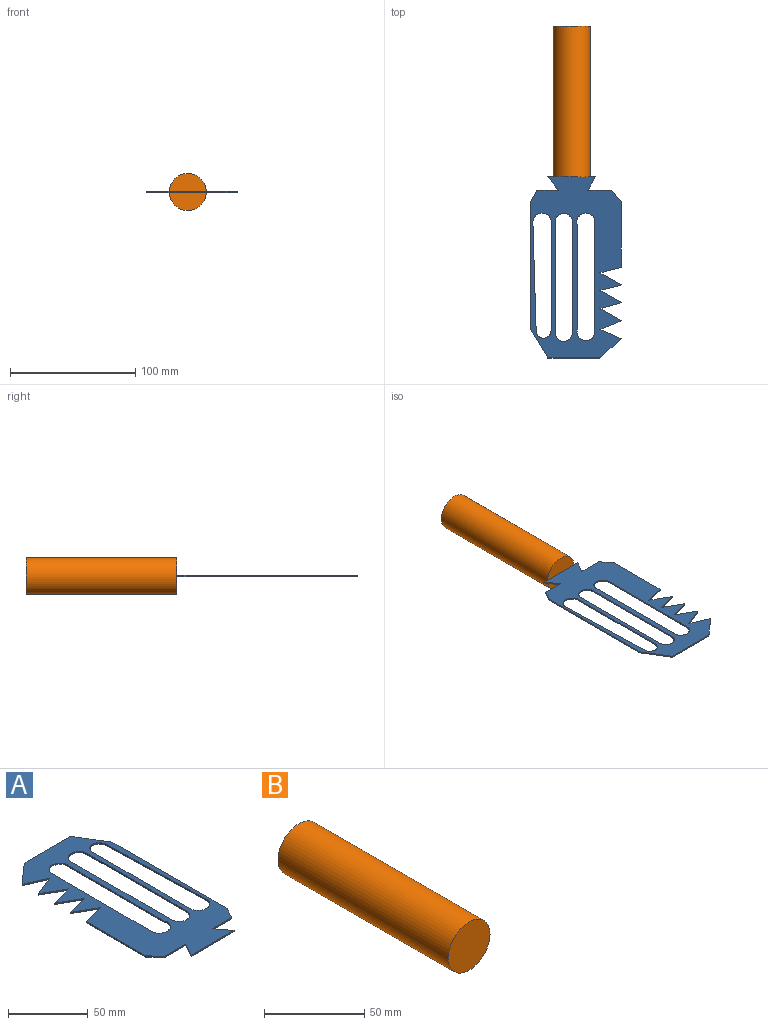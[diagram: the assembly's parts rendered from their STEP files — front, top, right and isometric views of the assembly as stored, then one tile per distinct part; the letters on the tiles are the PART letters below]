
ASSEMBLY  parts=2 mates=1
PART A: 34 faces, bbox 72.3x144.6x1 mm
  f0: plane 144.64x72.27mm, normal (0,0,1), area 5191.7mm2, adj f2,f3,f4,f5,f6,f7,f8,f9
  f1: plane 144.64x72.27mm, normal (0,0,-1), area 5191.7mm2, adj f2,f3,f4,f5,f6,f7,f8,f9
  f2: plane 8.78x4.98mm, normal (0.87,-0.49,0), area 10.1mm2, adj f0,f1,f3,f21
  f3: plane 102.2x1mm, normal (1,0,0), area 102.2mm2, adj f0,f1,f2,f4
  f4: plane 22.72x13.76mm, normal (0.86,0.52,0), area 26.6mm2, adj f0,f1,f3,f5
  f5: plane 41.27x1mm, normal (0,1,0), area 41.3mm2, adj f0,f1,f4,f6
  f6: plane 17.25x15.22mm, normal (-0.66,0.75,0), area 23mm2, adj f0,f1,f5,f7
  f7: plane 17.02x7.5mm, normal (-0.4,-0.91,0), area 18.6mm2, adj f0,f1,f6,f8
  f8: plane 17.02x6.98mm, normal (-0.38,0.93,0), area 18.4mm2, adj f0,f1,f7,f9
  f9: plane 17.02x9.65mm, normal (-0.49,-0.87,0), area 19.6mm2, adj f0,f1,f8,f10
  f10: plane 17.02x4.83mm, normal (-0.27,0.96,0), area 17.7mm2, adj f0,f1,f9,f11
  f11: plane 17.02x9.65mm, normal (-0.49,-0.87,0), area 19.6mm2, adj f0,f1,f10,f12
  f12: plane 17.02x4.39mm, normal (-0.25,0.97,0), area 17.6mm2, adj f0,f1,f11,f13
  f13: plane 17.02x9.65mm, normal (-0.49,-0.87,0), area 19.6mm2, adj f0,f1,f12,f14
  f14: plane 17.02x4.44mm, normal (-0.25,0.97,0), area 17.6mm2, adj f0,f1,f13,f15
  f15: plane 52.6x1mm, normal (-1,0,0), area 52.6mm2, adj f0,f1,f14,f16
  f16: plane 8.78x7.8mm, normal (-0.75,-0.66,0), area 11.7mm2, adj f0,f1,f15,f17
  f17: plane 18.92x1mm, normal (0,-1,0), area 18.9mm2, adj f0,f1,f16,f18
  f18: plane 10.94x6.21mm, normal (-0.87,0.49,0), area 12.6mm2, adj f0,f1,f17,f19
  f19: plane 38x1mm, normal (0,-1,0), area 38mm2, adj f0,f1,f18,f20
  f20: plane 10.94x8.15mm, normal (0.8,0.6,0), area 13.6mm2, adj f0,f1,f19,f21
  f21: plane 16.93x1mm, normal (0,-1,0), area 16.9mm2, adj f0,f1,f2,f20
  f22: plane 89.33x1mm, normal (-1,0,0), area 89.3mm2, adj f0,f1,f23,f25
  f23: cylinder r=6.78mm len=13.55mm, axis (0,0,1), area 21.3mm2, adj f0,f1,f22,f24
  f24: plane 89.33x1mm, normal (1,0,0), area 89.3mm2, adj f0,f1,f23,f25
  f25: cylinder r=6.86mm len=13.55mm, axis (0,0,1), area 19.4mm2, adj f0,f1,f22,f24
  f26: plane 85.09x2.57mm, normal (-1,-0.03,0), area 85.1mm2, adj f0,f1,f27,f29
  f27: cylinder r=5.97mm len=11.95mm, axis (0,0,1), area 19.7mm2, adj f0,f1,f26,f28
  f28: plane 86.18x1mm, normal (1,0,0), area 86.2mm2, adj f0,f1,f27,f29
  f29: cylinder r=7.37mm len=14.73mm, axis (0,0,1), area 23.4mm2, adj f0,f1,f26,f28
  f30: cylinder r=7.03mm len=14.05mm, axis (0,0,1), area 26.1mm2, adj f0,f1,f31,f33
  f31: plane 86.16x1mm, normal (1,0,0), area 86.2mm2, adj f0,f1,f30,f32
  f32: cylinder r=7.09mm len=14.18mm, axis (0,0,1), area 24.9mm2, adj f0,f1,f31,f33
  f33: plane 82.74x1mm, normal (-1,0,0), area 82.7mm2, adj f0,f1,f30,f32
PART B: 3 faces, bbox 29.5x120x29.5 mm
  f0: cylinder r=14.76mm len=120mm, axis (0,1,0), area 11125.2mm2, adj f1,f2
  f1: plane 29.51x29.51mm, normal (0,-1,0), area 684mm2, adj f0
  f2: plane 29.51x29.51mm, normal (0,1,0), area 684mm2, adj f0
PLACE A rot(axis=(0,0,1),180deg) t=(-70.39,-270.04,-12.17)mm
PLACE B t=(-64.05,-91.23,-11.67)mm
MATE fastened A.f19 <-> B.f0  axis (0,1,0) through (-64.05,-211.23,-11.67)mm
